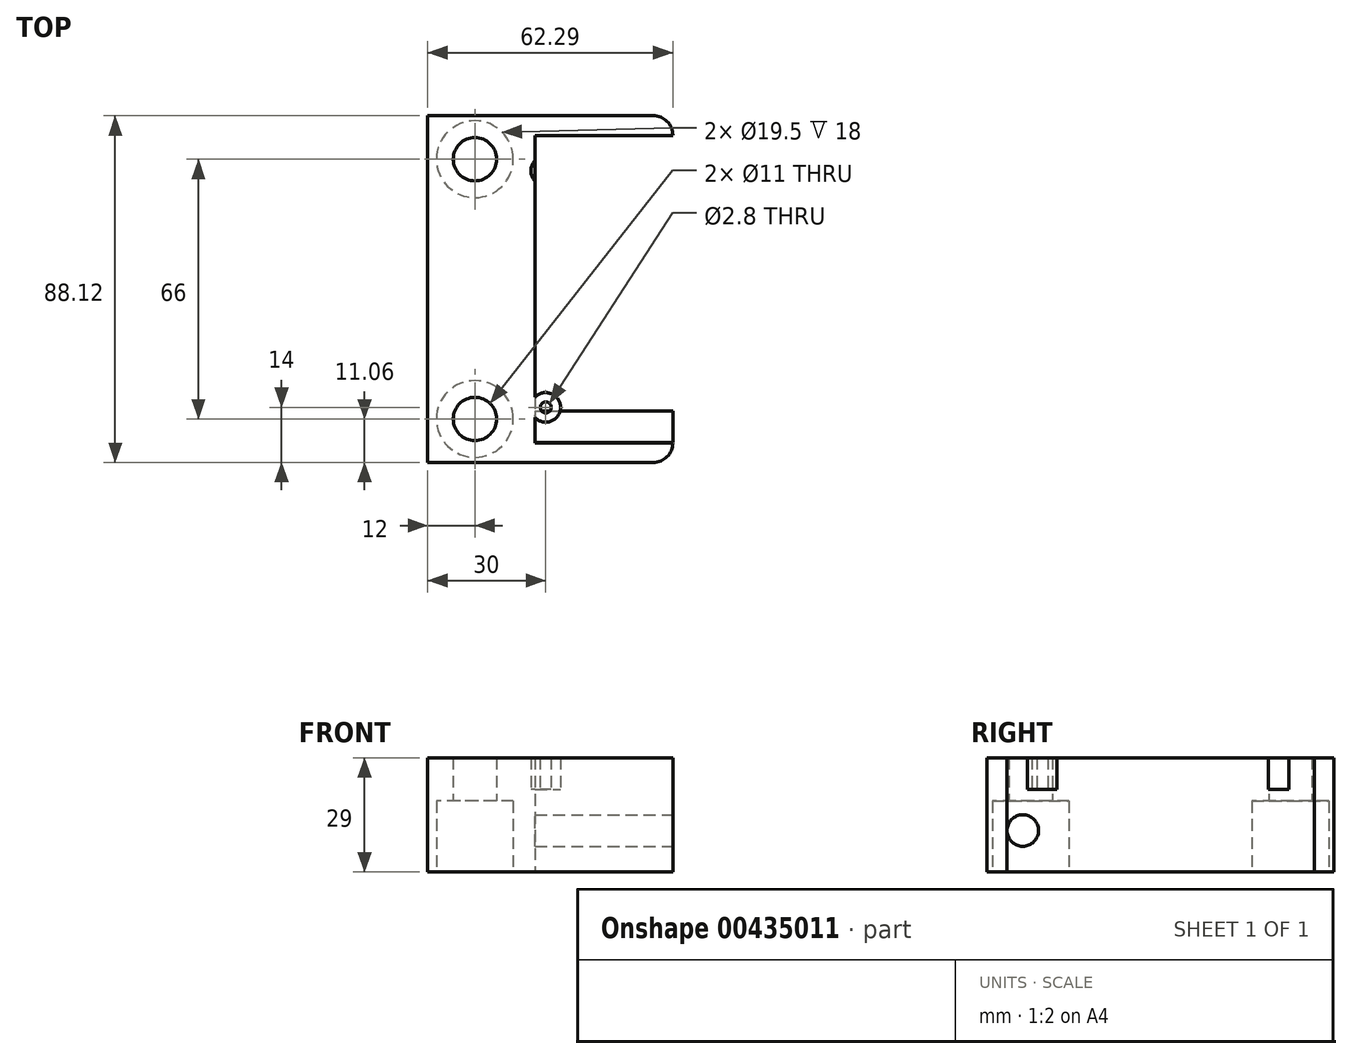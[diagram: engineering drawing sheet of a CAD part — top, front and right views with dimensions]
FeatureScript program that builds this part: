
annotation { "Feature Type Name" : "Feature", "Feature Type Description" : "" }
export const myFeature = defineFeature(function(context is Context, id is Id, definition is map)
    precondition{}
    {
        {
            var Q0;
            Q0=qCreatedBy(makeId("Top.planeOp"),FACE);
            var sketch = newSketch(context, id + "F0", { "sketchPlane" : qUnion([Q0])});
            skLineSegment(sketch, "E0", {"start": v(26.75, 0) * mm, "end": v(38, 0) * mm});
            skCircle(sketch, "E1", {"center": v(38, 0) * mm, "radius": 11.25 * mm});
            skLineSegment(sketch, "E2", {"start": v(0, 0) * mm, "end": v(0, 33) * mm});
            skLineSegment(sketch, "E3", {"start": v(0, 0) * mm, "end": v(0, -33) * mm});
            skLineSegment(sketch, "E4.bottom", {"start": v(0, 27) * mm, "end": v(0, 27) * mm});
            skLineSegment(sketch, "E4.top", {"start": v(0, -27) * mm, "end": v(0, -27) * mm});
            skCircle(sketch, "E5", {"center": v(0, -33) * mm, "radius": 9.75 * mm});
            skCircle(sketch, "E6", {"center": v(0, 33) * mm, "radius": 9.75 * mm});
            skLineSegment(sketch, "E7", {"start": v(0, 0) * mm, "end": v(26.75, 0) * mm});
            skLineSegment(sketch, "E8.bottom", {"start": v(21.5, 21.5) * mm, "end": v(21.48, 21.5) * mm});
            skPoint(sketch, "E8.middle", {"position": v(0, 0) * mm});
            skLineSegment(sketch, "E9.right", {"start": v(50.3, 23.56) * mm, "end": v(50.3, -23.56) * mm});
            skCircle(sketch, "E10", {"center": v(0, 33) * mm, "radius": 5.5 * mm});
            skCircle(sketch, "E11", {"center": v(0, -33) * mm, "radius": 5.5 * mm});
            skLineSegment(sketch, "E12", {"start": v(50.3, -39.06) * mm, "end": v(50.3, -23.56) * mm});
            skLineSegment(sketch, "E13", {"start": v(50.3, 39.06) * mm, "end": v(50.3, 23.56) * mm});
            skPoint(sketch, "E14.visualSharp", {"position": v(50.3, -44.06) * mm});
            skArc(sketch, "E14.filletArc", {"start": v(45.3, -44.06) * mm, "mid": v(48.83, -42.6) * mm, "end": v(50.3, -39.06) * mm});
            skPoint(sketch, "E15.visualSharp", {"position": v(50.3, 44.06) * mm});
            skArc(sketch, "E15.filletArc", {"start": v(50.3, 39.06) * mm, "mid": v(48.83, 42.6) * mm, "end": v(45.3, 44.06) * mm});
            skLineSegment(sketch, "E16", {"start": v(0, 0) * mm, "end": v(-12, 0) * mm, "construction": true});
            skLineSegment(sketch, "E17", {"start": v(-12, 0) * mm, "end": v(-12, 44.06) * mm});
            skLineSegment(sketch, "E18", {"start": v(-12, 44.06) * mm, "end": v(-12, -44.06) * mm});
            skLineSegment(sketch, "E19", {"start": v(-12, -44.06) * mm, "end": v(45.3, -44.06) * mm});
            skLineSegment(sketch, "E20", {"start": v(-12, 44.06) * mm, "end": v(45.3, 44.06) * mm});
            skSolve(sketch);
        }
        {
            var Q0;
            Q0=makeQuery(id+"F0.imprint","IMPRINT",FACE,{"disambiguationData":[TD([[makeQuery(id+"F0.imprint","IMPRINT",EDGE,{"derivedFrom":sQuery(id+"F0.wireOp",EDGE,"E1")}),-1.0]])]});
            var Q1;
            Q1=makeQuery(id+"F0.imprint","IMPRINT",FACE,{"disambiguationData":[TD([[makeQuery(id+"F0.imprint","IMPRINT",EDGE,{"derivedFrom":sQuery(id+"F0.wireOp",EDGE,"7569d964-31c0-40f6-a892-1a6ad66e8234")}),-1.0]])]});
            var Q2;
            Q2=makeQuery(id+"F0.imprint","IMPRINT",FACE,{"disambiguationData":[TD([[makeQuery(id+"F0.imprint","IMPRINT",EDGE,{"derivedFrom":sQuery(id+"F0.wireOp",EDGE,"e01d2da0-1d26-4bb3-a429-6a2a41ea2c41")}),1.0]])]});
            var Q3;
            Q3=makeQuery(id+"F0.imprint","IMPRINT",FACE,{"disambiguationData":[TD([[makeQuery(id+"F0.imprint","IMPRINT",EDGE,{"derivedFrom":sQuery(id+"F0.wireOp",EDGE,"7569d964-31c0-40f6-a892-1a6ad66e8234")}),1.0]])]});
            var Q4;
            Q4=makeQuery(id+"F0.imprint","IMPRINT",FACE,{"disambiguationData":[TD([[makeQuery(id+"F0.imprint","IMPRINT",EDGE,{"derivedFrom":sQuery(id+"F0.wireOp",EDGE,"E5")}),-1.0]])]});
            extrude(context, id + "F1", {"entities" : qUnion([Q0, Q1, Q2, Q3, Q4]), "depth" : 2 * mm});
        }
        {
            var Q0;
            Q0=makeQuery(id+"F1.opExtrude","CAP_FACE",FACE,{"disambiguationData":[OSD([sQuery(id+"F0.wireOp",EDGE,"E1"),sQuery(id+"F0.wireOp",EDGE,"7569d964-31c0-40f6-a892-1a6ad66e8234"),sQuery(id+"F0.wireOp",EDGE,"e01d2da0-1d26-4bb3-a429-6a2a41ea2c41"),sQuery(id+"F0.wireOp",EDGE,"E8.bottom"),sQuery(id+"F0.wireOp",EDGE,"E8.top"),sQuery(id+"F0.wireOp",EDGE,"E8.left"),sQuery(id+"F0.wireOp",EDGE,"E8.right"),sQuery(id+"F0.wireOp",EDGE,"65e44e43-ea3c-4f37-955c-a272e1c85011"),sQuery(id+"F0.wireOp",EDGE,"12dd65b3-ea4f-403a-bbc6-4b277dfa3eb1"),sQuery(id+"F0.wireOp",EDGE,"E9.right"),sQuery(id+"F0.wireOp",EDGE,"618431a0-3797-4b71-b07f-beab4b43895c"),sQuery(id+"F0.wireOp",EDGE,"eef4be6b-fde0-4edc-b3ba-83a9abe2952a"),sQuery(id+"F0.wireOp",EDGE,"MserTwVI-edoU-uXqc-Z8qt-4XlbS5gjHU0l.bottom"),sQuery(id+"F0.wireOp",EDGE,"MserTwVI-edoU-uXqc-Z8qt-4XlbS5gjHU0l.top"),sQuery(id+"F0.wireOp",EDGE,"MserTwVI-edoU-uXqc-Z8qt-4XlbS5gjHU0l.left"),sQuery(id+"F0.wireOp",EDGE,"MserTwVI-edoU-uXqc-Z8qt-4XlbS5gjHU0l.right")])],"isStart":false});
            var sketch = newSketch(context, id + "F2", { "sketchPlane" : qUnion([Q0])});
            skCircle(sketch, "E21", {"center": v(38, 0) * mm, "radius": 5.1 * mm});
            skLineSegment(sketch, "E22", {"start": v(38, 0) * mm, "end": v(38, 8) * mm});
            skCircle(sketch, "E23", {"center": v(38, 8) * mm, "radius": 2 * mm});
            skCircle(sketch, "E24.MirrorC", {"center": v(38, -8) * mm, "radius": 2 * mm});
            skLineSegment(sketch, "E25", {"start": v(38, 0) * mm, "end": v(46, 0) * mm});
            skCircle(sketch, "E26", {"center": v(46, 0) * mm, "radius": 2 * mm});
            skCircle(sketch, "E27.MirrorC", {"center": v(30, 0) * mm, "radius": 2 * mm});
            skCircle(sketch, "E28", {"center": v(0, -33) * mm, "radius": 9.75 * mm});
            skCircle(sketch, "E29", {"center": v(0, 33) * mm, "radius": 9.75 * mm});
            skSolve(sketch);
        }
        {
            var Q0;
            Q0=makeQuery(id+"F2.imprint","IMPRINT",FACE,{"disambiguationData":[TD([[makeQuery(id+"F2.imprint","IMPRINT",EDGE,{"derivedFrom":sQuery(id+"F2.wireOp",EDGE,"E28")}),-1.0]])]});
            var Q1;
            Q1=makeQuery(id+"F2.imprint","IMPRINT",FACE,{"disambiguationData":[TD([[makeQuery(id+"F2.imprint","IMPRINT",EDGE,{"derivedFrom":sQuery(id+"F2.wireOp",EDGE,"E23")}),-1.0]])]});
            extrude(context, id + "F3", {"entities" : qUnion([Q0, Q1]), "operationType" : NewBodyOperationType.ADD, "depth" : 16 * mm});
        }
        {
            var Q0;
            Q0=makeQuery(id+"F3.opExtrude","CAP_FACE",FACE,{"disambiguationData":[OSD([sQuery(id+"F0.wireOp",EDGE,"E8.bottom"),sQuery(id+"F0.wireOp",EDGE,"E8.top"),sQuery(id+"F0.wireOp",EDGE,"E8.left"),sQuery(id+"F0.wireOp",EDGE,"E8.right"),sQuery(id+"F0.wireOp",EDGE,"65e44e43-ea3c-4f37-955c-a272e1c85011"),sQuery(id+"F0.wireOp",EDGE,"12dd65b3-ea4f-403a-bbc6-4b277dfa3eb1"),sQuery(id+"F0.wireOp",EDGE,"E9.right"),sQuery(id+"F0.wireOp",EDGE,"618431a0-3797-4b71-b07f-beab4b43895c"),sQuery(id+"F0.wireOp",EDGE,"eef4be6b-fde0-4edc-b3ba-83a9abe2952a"),sQuery(id+"F0.wireOp",EDGE,"MserTwVI-edoU-uXqc-Z8qt-4XlbS5gjHU0l.bottom"),sQuery(id+"F0.wireOp",EDGE,"MserTwVI-edoU-uXqc-Z8qt-4XlbS5gjHU0l.top"),sQuery(id+"F0.wireOp",EDGE,"MserTwVI-edoU-uXqc-Z8qt-4XlbS5gjHU0l.left"),sQuery(id+"F0.wireOp",EDGE,"MserTwVI-edoU-uXqc-Z8qt-4XlbS5gjHU0l.right"),sQuery(id+"F2.wireOp",EDGE,"E21"),sQuery(id+"F2.wireOp",EDGE,"E23"),sQuery(id+"F2.wireOp",EDGE,"E24.MirrorC"),sQuery(id+"F2.wireOp",EDGE,"E26"),sQuery(id+"F2.wireOp",EDGE,"E27.MirrorC"),sQuery(id+"F2.wireOp",EDGE,"E28"),sQuery(id+"F2.wireOp",EDGE,"E29")])],"isStart":false});
            var sketch = newSketch(context, id + "F4", { "sketchPlane" : qUnion([Q0])});
            skPoint(sketch, "E30.endSnap0", {"position": v(21.5, 0) * mm});
            skSolve(sketch);
        }
        {
            var Q0;
            Q0=makeQuery(id+"F4.imprint","IMPRINT",FACE,{"disambiguationData":[TD([[makeQuery(id+"F4.imprint","IMPRINT",EDGE,{"derivedFrom":makeQuery(id+"F3.opExtrude","CAP_EDGE",EDGE,{"disambiguationData":[OSD([sQuery(id+"F2.wireOp",EDGE,"E21")])],"isStart":false})}),-1.0]])]});
            var Q1;
            Q1=makeQuery(id+"F4.imprint","IMPRINT",FACE,{"disambiguationData":[TD([[makeQuery(id+"F4.imprint","IMPRINT",EDGE,{"derivedFrom":sQuery(id+"F4.wireOp",EDGE,"W1AygPTk-y3eS-NhdS-xGVm-LvzuyxNYVIWd")}),-1.0]])]});
            var Q2;
            Q2=makeQuery(id+"F4.imprint","IMPRINT",FACE,{"disambiguationData":[TD([[makeQuery(id+"F4.imprint","IMPRINT",EDGE,{"derivedFrom":makeQuery(id+"F3.opExtrude","CAP_EDGE",EDGE,{"disambiguationData":[OSD([sQuery(id+"F2.wireOp",EDGE,"E28")])],"isStart":false})}),1.0]])]});
            var Q3;
            Q3=makeQuery(id+"F4.imprint","IMPRINT",FACE,{"disambiguationData":[TD([[makeQuery(id+"F4.imprint","IMPRINT",EDGE,{"derivedFrom":makeQuery(id+"F3.opExtrude","CAP_EDGE",EDGE,{"disambiguationData":[OSD([sQuery(id+"F2.wireOp",EDGE,"E29")])],"isStart":false})}),1.0]])]});
            extrude(context, id + "F5", {"entities" : qUnion([Q0, Q1, Q2, Q3]), "operationType" : NewBodyOperationType.ADD, "depth" : 3 * mm});
        }
        {
            var Q0;
            {var subQ0=sQuery(id+"F0.wireOp",EDGE,"E9.right");Q0=makeQuery(id+"F5.boolean.opBoolean","MERGE",FACE,{"derivedFrom":[makeQuery(id+"F3.boolean.opBoolean","MERGE",FACE,{"derivedFrom":[makeQuery(id+"F1.opExtrude","SWEPT_FACE",FACE,{"disambiguationData":[OSD([subQ0])]}),makeQuery(id+"F3.opExtrude","SWEPT_FACE",FACE,{"disambiguationData":[OSD([subQ0])]})]}),makeQuery(id+"F5.opExtrude","SWEPT_FACE",FACE,{"disambiguationData":[OSD([subQ0])]})]});}
            var sketch = newSketch(context, id + "F6", { "sketchPlane" : qUnion([Q0])});
            skLineSegment(sketch, "E31", {"start": v(0, 0) * mm, "end": v(0, 10.5) * mm, "construction": true});
            skLineSegment(sketch, "E32", {"start": v(0, 10.5) * mm, "end": v(35, 10.5) * mm, "construction": true});
            skPoint(sketch, "E32.endSnap0", {"position": v(-39.06, 10.5) * mm});
            skCircle(sketch, "E33", {"center": v(35, 10.5) * mm, "radius": 4 * mm});
            skCircle(sketch, "E34.MirrorC", {"center": v(-35, 10.5) * mm, "radius": 4 * mm});
            skSolve(sketch);
        }
        {
            var Q0;
            Q0=makeQuery(id+"F0.imprint","IMPRINT",FACE,{"disambiguationData":[TD([[makeQuery(id+"F0.imprint","IMPRINT",EDGE,{"derivedFrom":sQuery(id+"F0.wireOp",EDGE,"E11")}),1.0]])]});
            var Q1;
            Q1=makeQuery(id+"F0.imprint","IMPRINT",FACE,{"disambiguationData":[TD([[makeQuery(id+"F0.imprint","IMPRINT",EDGE,{"derivedFrom":sQuery(id+"F0.wireOp",EDGE,"E10")}),1.0]])]});
            extrude(context, id + "F7", {"entities" : qUnion([Q0, Q1]), "operationType" : NewBodyOperationType.REMOVE, "oppositeDirection" : true, "depth" : -40 * mm});
        }
        {
            var Q0;
            Q0=makeQuery(id+"F6.imprint","IMPRINT",FACE,{"disambiguationData":[TD([[makeQuery(id+"F6.imprint","IMPRINT",EDGE,{"derivedFrom":sQuery(id+"F6.wireOp",EDGE,"E33")}),1.0]])]});
            var Q1;
            Q1=makeQuery(id+"F6.imprint","IMPRINT",FACE,{"disambiguationData":[TD([[makeQuery(id+"F6.imprint","IMPRINT",EDGE,{"derivedFrom":sQuery(id+"F6.wireOp",EDGE,"E34.MirrorC")}),-1.0]])]});
            extrude(context, id + "F8", {"entities" : qUnion([Q0, Q1]), "operationType" : NewBodyOperationType.REMOVE, "oppositeDirection" : true, "depth" : 35 * mm});
        }
        {
            var Q0;
            Q0=makeQuery(id+"F5.opExtrude","CAP_FACE",FACE,{"disambiguationData":[OSD([sQuery(id+"F0.wireOp",EDGE,"E9.right"),sQuery(id+"F0.wireOp",EDGE,"E12"),sQuery(id+"F0.wireOp",EDGE,"E13"),sQuery(id+"F0.wireOp",EDGE,"E14.filletArc"),sQuery(id+"F0.wireOp",EDGE,"E15.filletArc"),sQuery(id+"F0.wireOp",EDGE,"E18"),sQuery(id+"F0.wireOp",EDGE,"E19"),sQuery(id+"F0.wireOp",EDGE,"E20"),sQuery(id+"F2.wireOp",EDGE,"E21"),sQuery(id+"F2.wireOp",EDGE,"E23"),sQuery(id+"F2.wireOp",EDGE,"E24.MirrorC"),sQuery(id+"F2.wireOp",EDGE,"E26"),sQuery(id+"F2.wireOp",EDGE,"E27.MirrorC")])],"isStart":false});
            var sketch = newSketch(context, id + "F9", { "sketchPlane" : qUnion([Q0])});
            skLineSegment(sketch, "E35", {"start": v(18, 0) * mm, "end": v(18, -44.06) * mm, "construction": true});
            skLineSegment(sketch, "E36", {"start": v(18, -44.06) * mm, "end": v(18, -30.06) * mm, "construction": true});
            skCircle(sketch, "E37", {"center": v(18, -30.06) * mm, "radius": 3.75 * mm});
            skCircle(sketch, "E38.MirrorC", {"center": v(18, 30.06) * mm, "radius": 3.75 * mm});
            skCircle(sketch, "E39", {"center": v(18, -30.06) * mm, "radius": 1.4 * mm});
            skCircle(sketch, "E40.MirrorC", {"center": v(18, 30.06) * mm, "radius": 1.4 * mm});
            skSolve(sketch);
        }
        {
            var Q0;
            Q0=makeQuery(id+"F9.imprint","IMPRINT",FACE,{"disambiguationData":[TD([[makeQuery(id+"F9.imprint","IMPRINT",EDGE,{"derivedFrom":sQuery(id+"F9.wireOp",EDGE,"E37")}),1.0]])]});
            var Q1;
            Q1=makeQuery(id+"F9.imprint","IMPRINT",FACE,{"disambiguationData":[TD([[makeQuery(id+"F9.imprint","IMPRINT",EDGE,{"derivedFrom":sQuery(id+"F9.wireOp",EDGE,"E38.MirrorC")}),-1.0]])]});
            extrude(context, id + "F10", {"entities" : qUnion([Q0, Q1]), "operationType" : NewBodyOperationType.ADD, "depth" : 8 * mm});
        }
    });
